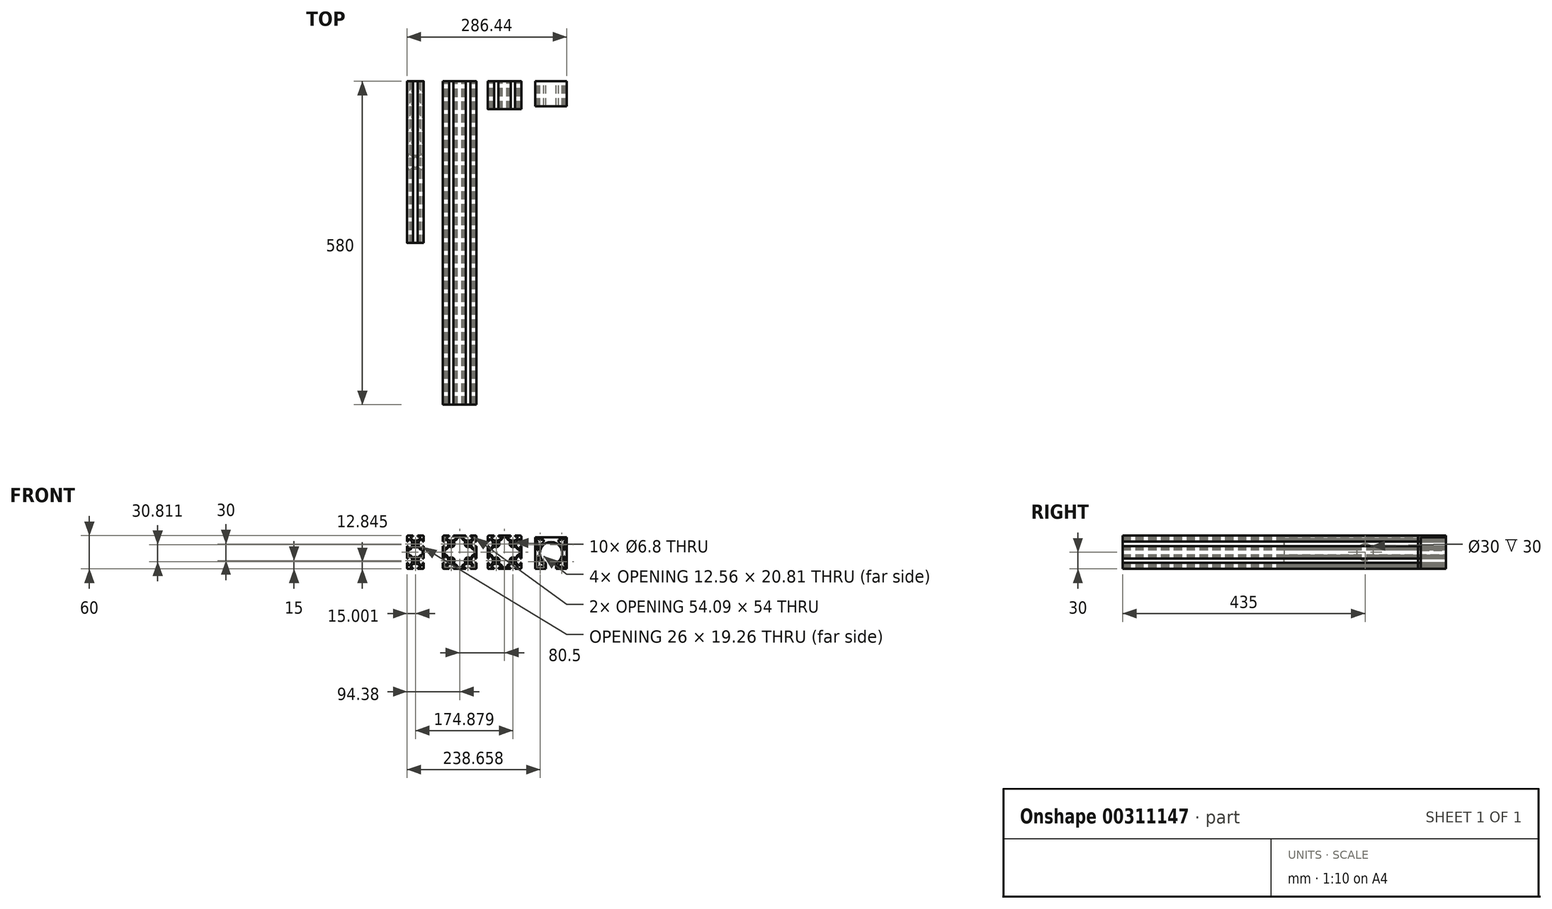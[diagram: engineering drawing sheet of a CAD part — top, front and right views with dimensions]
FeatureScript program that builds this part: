
annotation { "Feature Type Name" : "Feature", "Feature Type Description" : "" }
export const myFeature = defineFeature(function(context is Context, id is Id, definition is map)
    precondition{}
    {
        {
            var Q0;
            Q0=qCreatedBy(makeId("Front.planeOp"),FACE);
            var sketch = newSketch(context, id + "F0", { "sketchPlane" : qUnion([Q0])});
            skLineSegment(sketch, "E0.bottom", {"start": v(-15, 15) * mm, "end": v(15, 15) * mm, "construction": true});
            skLineSegment(sketch, "E0.top", {"start": v(-15, -15) * mm, "end": v(15, -15) * mm, "construction": true});
            skLineSegment(sketch, "E0.left", {"start": v(-15, 15) * mm, "end": v(-15, -15) * mm, "construction": true});
            skLineSegment(sketch, "E0.right", {"start": v(15, 15) * mm, "end": v(15, -15) * mm, "construction": true});
            skCircle(sketch, "E1", {"center": v(-15, 15) * mm, "radius": 3.4 * mm});
            skCircle(sketch, "E2", {"center": v(15, 15) * mm, "radius": 3.4 * mm});
            skCircle(sketch, "E3", {"center": v(15, -15) * mm, "radius": 3.4 * mm});
            skCircle(sketch, "E4", {"center": v(-15, -15) * mm, "radius": 3.4 * mm});
            skLineSegment(sketch, "E5", {"start": v(-28, 30) * mm, "end": v(-19, 30) * mm});
            skLineSegment(sketch, "E6", {"start": v(-19, 30) * mm, "end": v(-19, 28) * mm});
            skLineSegment(sketch, "E7", {"start": v(-19, 28) * mm, "end": v(-23.25, 28) * mm});
            skLineSegment(sketch, "E8", {"start": v(-23.25, 28) * mm, "end": v(-23.25, 25) * mm});
            skLineSegment(sketch, "E9", {"start": v(-23.25, 25) * mm, "end": v(-19, 21) * mm});
            skLineSegment(sketch, "E10.MirrorCS", {"start": v(-11, 30) * mm, "end": v(-11, 28) * mm});
            skLineSegment(sketch, "E11.MirrorCS", {"start": v(-11, 28) * mm, "end": v(-6.75, 28) * mm});
            skLineSegment(sketch, "E12.MirrorCS", {"start": v(-6.75, 28) * mm, "end": v(-6.75, 25) * mm});
            skLineSegment(sketch, "E13.MirrorCS", {"start": v(-6.75, 25) * mm, "end": v(-11, 21) * mm});
            skLineSegment(sketch, "E14", {"start": v(-19, 21) * mm, "end": v(-11, 21) * mm});
            skLineSegment(sketch, "E15", {"start": v(-4.08, 0) * mm, "end": v(-10, 0) * mm, "construction": true});
            skLineSegment(sketch, "E16", {"start": v(0, -4) * mm, "end": v(0, -10.45) * mm, "construction": true});
            skLineSegment(sketch, "E17.MirrorCS", {"start": v(19, 30) * mm, "end": v(19, 28) * mm});
            skLineSegment(sketch, "E18.MirrorCS", {"start": v(11, 30) * mm, "end": v(11, 28) * mm});
            skLineSegment(sketch, "E19.MirrorCS", {"start": v(23.25, 28) * mm, "end": v(23.25, 25) * mm});
            skLineSegment(sketch, "E20.MirrorCS", {"start": v(28, 30) * mm, "end": v(19, 30) * mm});
            skLineSegment(sketch, "E21.MirrorCS", {"start": v(19, 21) * mm, "end": v(11, 21) * mm});
            skLineSegment(sketch, "E22.MirrorCS", {"start": v(23.25, 25) * mm, "end": v(19, 21) * mm});
            skLineSegment(sketch, "E23.MirrorCS", {"start": v(6.75, 28) * mm, "end": v(6.75, 25) * mm});
            skLineSegment(sketch, "E24.MirrorCS", {"start": v(19, 28) * mm, "end": v(23.25, 28) * mm});
            skLineSegment(sketch, "E25.MirrorCS", {"start": v(6.75, 25) * mm, "end": v(11, 21) * mm});
            skLineSegment(sketch, "E26.MirrorCS", {"start": v(11, 28) * mm, "end": v(6.75, 28) * mm});
            skLineSegment(sketch, "E27.MirrorCS", {"start": v(19, -30) * mm, "end": v(19, -28) * mm});
            skLineSegment(sketch, "E28.MirrorCS", {"start": v(-19, -30) * mm, "end": v(-19, -28) * mm});
            skLineSegment(sketch, "E29.MirrorCS", {"start": v(-11, -30) * mm, "end": v(-11, -28) * mm});
            skLineSegment(sketch, "E30.MirrorCS", {"start": v(11, -30) * mm, "end": v(11, -28) * mm});
            skLineSegment(sketch, "E31.MirrorCS", {"start": v(23.25, -28) * mm, "end": v(23.25, -25) * mm});
            skLineSegment(sketch, "E32.MirrorCS", {"start": v(-28, -30) * mm, "end": v(-19, -30) * mm});
            skLineSegment(sketch, "E33.MirrorCS", {"start": v(19, -21) * mm, "end": v(11, -21) * mm});
            skLineSegment(sketch, "E34.MirrorCS", {"start": v(-19, -28) * mm, "end": v(-23.25, -28) * mm});
            skLineSegment(sketch, "E35.MirrorCS", {"start": v(6.75, -28) * mm, "end": v(6.75, -25) * mm});
            skLineSegment(sketch, "E36.MirrorCS", {"start": v(-23.25, -25) * mm, "end": v(-19, -21) * mm});
            skLineSegment(sketch, "E37.MirrorCS", {"start": v(-11, -28) * mm, "end": v(-6.75, -28) * mm});
            skLineSegment(sketch, "E38.MirrorCS", {"start": v(6.75, -25) * mm, "end": v(11, -21) * mm});
            skLineSegment(sketch, "E39.MirrorCS", {"start": v(-6.75, -25) * mm, "end": v(-11, -21) * mm});
            skLineSegment(sketch, "E40.MirrorCS", {"start": v(28, -30) * mm, "end": v(19, -30) * mm});
            skLineSegment(sketch, "E41.MirrorCS", {"start": v(-6.75, -28) * mm, "end": v(-6.75, -25) * mm});
            skLineSegment(sketch, "E42.MirrorCS", {"start": v(-19, -21) * mm, "end": v(-11, -21) * mm});
            skLineSegment(sketch, "E43.MirrorCS", {"start": v(19, -28) * mm, "end": v(23.25, -28) * mm});
            skLineSegment(sketch, "E44.MirrorCS", {"start": v(11, -28) * mm, "end": v(6.75, -28) * mm});
            skLineSegment(sketch, "E45.MirrorCS", {"start": v(23.25, -25) * mm, "end": v(19, -21) * mm});
            skLineSegment(sketch, "E46.MirrorCS", {"start": v(-23.25, -28) * mm, "end": v(-23.25, -25) * mm});
            skLineSegment(sketch, "E47", {"start": v(-30, 28) * mm, "end": v(-30, 19) * mm});
            skLineSegment(sketch, "E48", {"start": v(-30, 19) * mm, "end": v(-28, 19) * mm});
            skLineSegment(sketch, "E49", {"start": v(-28, 19) * mm, "end": v(-28, 23.25) * mm});
            skLineSegment(sketch, "E50", {"start": v(-28, 23.25) * mm, "end": v(-25, 23.25) * mm});
            skLineSegment(sketch, "E51", {"start": v(-25, 23.25) * mm, "end": v(-21, 19) * mm});
            skLineSegment(sketch, "E52.MirrorCS", {"start": v(-30, 11) * mm, "end": v(-28, 11) * mm});
            skLineSegment(sketch, "E53.MirrorCS", {"start": v(-28, 11) * mm, "end": v(-28, 6.75) * mm});
            skLineSegment(sketch, "E54.MirrorCS", {"start": v(-28, 6.75) * mm, "end": v(-25, 6.75) * mm});
            skLineSegment(sketch, "E55.MirrorCS", {"start": v(-25, 6.75) * mm, "end": v(-21, 11) * mm});
            skLineSegment(sketch, "E56", {"start": v(-21, 11) * mm, "end": v(-21, 19) * mm});
            skLineSegment(sketch, "E57.MirrorCS", {"start": v(-28, -6.75) * mm, "end": v(-25, -6.75) * mm});
            skLineSegment(sketch, "E58.MirrorCS", {"start": v(-28, -11) * mm, "end": v(-28, -6.75) * mm});
            skLineSegment(sketch, "E59.MirrorCS", {"start": v(-25, -6.75) * mm, "end": v(-21, -11) * mm});
            skLineSegment(sketch, "E60.MirrorCS", {"start": v(-21, -11) * mm, "end": v(-21, -19) * mm});
            skLineSegment(sketch, "E61.MirrorCS", {"start": v(-25, -23.25) * mm, "end": v(-21, -19) * mm});
            skLineSegment(sketch, "E62.MirrorCS", {"start": v(-28, -23.25) * mm, "end": v(-25, -23.25) * mm});
            skLineSegment(sketch, "E63.MirrorCS", {"start": v(-28, -19) * mm, "end": v(-28, -23.25) * mm});
            skLineSegment(sketch, "E64.MirrorCS", {"start": v(-30, -19) * mm, "end": v(-28, -19) * mm});
            skLineSegment(sketch, "E65.MirrorCS", {"start": v(-30, -11) * mm, "end": v(-28, -11) * mm});
            skLineSegment(sketch, "E66.MirrorCS", {"start": v(30, -11) * mm, "end": v(28, -11) * mm});
            skLineSegment(sketch, "E67.MirrorCS", {"start": v(28, -11) * mm, "end": v(28, -6.75) * mm});
            skLineSegment(sketch, "E68.MirrorCS", {"start": v(28, -6.75) * mm, "end": v(25, -6.75) * mm});
            skLineSegment(sketch, "E69.MirrorCS", {"start": v(25, -6.75) * mm, "end": v(21, -11) * mm});
            skLineSegment(sketch, "E70.MirrorCS", {"start": v(21, -11) * mm, "end": v(21, -19) * mm});
            skLineSegment(sketch, "E71.MirrorCS", {"start": v(25, -23.25) * mm, "end": v(21, -19) * mm});
            skLineSegment(sketch, "E72.MirrorCS", {"start": v(28, -23.25) * mm, "end": v(25, -23.25) * mm});
            skLineSegment(sketch, "E73.MirrorCS", {"start": v(28, -19) * mm, "end": v(28, -23.25) * mm});
            skLineSegment(sketch, "E74.MirrorCS", {"start": v(30, -19) * mm, "end": v(28, -19) * mm});
            skLineSegment(sketch, "E75.MirrorCS", {"start": v(28, 6.75) * mm, "end": v(25, 6.75) * mm});
            skLineSegment(sketch, "E76.MirrorCS", {"start": v(28, 11) * mm, "end": v(28, 6.75) * mm});
            skLineSegment(sketch, "E77.MirrorCS", {"start": v(30, 11) * mm, "end": v(28, 11) * mm});
            skLineSegment(sketch, "E78.MirrorCS", {"start": v(30, 19) * mm, "end": v(28, 19) * mm});
            skLineSegment(sketch, "E79.MirrorCS", {"start": v(28, 19) * mm, "end": v(28, 23.25) * mm});
            skLineSegment(sketch, "E80.MirrorCS", {"start": v(28, 23.25) * mm, "end": v(25, 23.25) * mm});
            skLineSegment(sketch, "E81.MirrorCS", {"start": v(25, 23.25) * mm, "end": v(21, 19) * mm});
            skLineSegment(sketch, "E82.MirrorCS", {"start": v(21, 11) * mm, "end": v(21, 19) * mm});
            skLineSegment(sketch, "E83.MirrorCS", {"start": v(25, 6.75) * mm, "end": v(21, 11) * mm});
            skLineSegment(sketch, "E84", {"start": v(-11, 30) * mm, "end": v(11, 30) * mm});
            skLineSegment(sketch, "E85", {"start": v(-30, 11) * mm, "end": v(-30, -11) * mm});
            skLineSegment(sketch, "E86", {"start": v(-30, -19) * mm, "end": v(-30, -28) * mm});
            skLineSegment(sketch, "E87", {"start": v(-11, -30) * mm, "end": v(11, -30) * mm});
            skLineSegment(sketch, "E88", {"start": v(30, -28) * mm, "end": v(30, -19) * mm});
            skLineSegment(sketch, "E89", {"start": v(30, -11) * mm, "end": v(30, 11) * mm});
            skLineSegment(sketch, "E90", {"start": v(30, 28) * mm, "end": v(30, 19) * mm});
            skLineSegment(sketch, "E91", {"start": v(-4.25, 27) * mm, "end": v(4.25, 27) * mm});
            skLineSegment(sketch, "E92", {"start": v(-4.25, 24.4) * mm, "end": v(-10.38, 18.63) * mm});
            skLineSegment(sketch, "E93", {"start": v(-4.25, 24.4) * mm, "end": v(-4.25, 27) * mm});
            skLineSegment(sketch, "E94.MirrorCS", {"start": v(4.25, 24.4) * mm, "end": v(10.38, 18.63) * mm});
            skLineSegment(sketch, "E95.MirrorCS", {"start": v(4.25, 24.4) * mm, "end": v(4.25, 27) * mm});
            skLineSegment(sketch, "E96.MirrorCS", {"start": v(-4.25, -24.4) * mm, "end": v(-10.38, -18.63) * mm});
            skLineSegment(sketch, "E97.MirrorCS", {"start": v(-4.25, -24.4) * mm, "end": v(-4.25, -27) * mm});
            skLineSegment(sketch, "E98.MirrorCS", {"start": v(-4.25, -27) * mm, "end": v(4.25, -27) * mm});
            skLineSegment(sketch, "E99.MirrorCS", {"start": v(4.25, -24.4) * mm, "end": v(4.25, -27) * mm});
            skLineSegment(sketch, "E100.MirrorCS", {"start": v(4.25, -24.4) * mm, "end": v(10.38, -18.63) * mm});
            skLineSegment(sketch, "E101", {"start": v(-27.04, -4.24) * mm, "end": v(-27.04, 4.26) * mm});
            skLineSegment(sketch, "E102", {"start": v(-24.45, -4.24) * mm, "end": v(-18.68, -10.37) * mm});
            skLineSegment(sketch, "E103", {"start": v(-24.45, -4.24) * mm, "end": v(-27.04, -4.24) * mm});
            skLineSegment(sketch, "E104.MirrorCS", {"start": v(-24.45, 4.26) * mm, "end": v(-18.68, 10.39) * mm});
            skLineSegment(sketch, "E105.MirrorCS", {"start": v(-24.45, 4.26) * mm, "end": v(-27.04, 4.26) * mm});
            skLineSegment(sketch, "E106.MirrorCS", {"start": v(27.04, -4.24) * mm, "end": v(27.04, 4.26) * mm});
            skLineSegment(sketch, "E107.MirrorCS", {"start": v(24.45, 4.26) * mm, "end": v(27.04, 4.26) * mm});
            skLineSegment(sketch, "E108.MirrorCS", {"start": v(24.45, 4.26) * mm, "end": v(18.68, 10.39) * mm});
            skLineSegment(sketch, "E109.MirrorCS", {"start": v(24.45, -4.24) * mm, "end": v(27.04, -4.24) * mm});
            skLineSegment(sketch, "E110.MirrorCS", {"start": v(24.45, -4.24) * mm, "end": v(18.68, -10.37) * mm});
            skArc(sketch, "E111", {"start": v(-18.68, 10.39) * mm, "mid": v(-10.85, 10.8) * mm, "end": v(-10.38, 18.63) * mm});
            skArc(sketch, "E112", {"start": v(10.38, 18.63) * mm, "mid": v(10.87, 10.83) * mm, "end": v(18.68, 10.39) * mm});
            skArc(sketch, "E113", {"start": v(18.68, -10.37) * mm, "mid": v(10.87, -10.83) * mm, "end": v(10.38, -18.63) * mm});
            skArc(sketch, "E114", {"start": v(-10.38, -18.63) * mm, "mid": v(-10.79, -10.75) * mm, "end": v(-18.68, -10.37) * mm});
            skLineSegment(sketch, "E115.bottom", {"start": v(65.5, 15) * mm, "end": v(95.5, 15) * mm, "construction": true});
            skLineSegment(sketch, "E115.top", {"start": v(65.5, -15) * mm, "end": v(95.5, -15) * mm, "construction": true});
            skLineSegment(sketch, "E115.left", {"start": v(65.5, 15) * mm, "end": v(65.5, -15) * mm, "construction": true});
            skLineSegment(sketch, "E115.right", {"start": v(95.5, 15) * mm, "end": v(95.5, -15) * mm, "construction": true});
            skCircle(sketch, "E116", {"center": v(65.5, 15) * mm, "radius": 3.4 * mm});
            skCircle(sketch, "E117", {"center": v(95.5, 15) * mm, "radius": 3.4 * mm});
            skCircle(sketch, "E118", {"center": v(95.5, -15) * mm, "radius": 3.4 * mm});
            skCircle(sketch, "E119", {"center": v(65.5, -15) * mm, "radius": 3.4 * mm});
            skLineSegment(sketch, "E120", {"start": v(52.5, 30) * mm, "end": v(61.5, 30) * mm});
            skLineSegment(sketch, "E121", {"start": v(61.5, 30) * mm, "end": v(61.5, 28) * mm});
            skLineSegment(sketch, "E122", {"start": v(61.5, 28) * mm, "end": v(57.25, 28) * mm});
            skLineSegment(sketch, "E123", {"start": v(57.25, 28) * mm, "end": v(57.25, 25) * mm});
            skLineSegment(sketch, "E124", {"start": v(57.25, 25) * mm, "end": v(61.5, 21) * mm});
            skLineSegment(sketch, "E125.MirrorCS", {"start": v(69.5, 30) * mm, "end": v(69.5, 28) * mm});
            skLineSegment(sketch, "E126.MirrorCS", {"start": v(69.5, 28) * mm, "end": v(73.75, 28) * mm});
            skLineSegment(sketch, "E127.MirrorCS", {"start": v(73.75, 28) * mm, "end": v(73.75, 25) * mm});
            skLineSegment(sketch, "E128.MirrorCS", {"start": v(73.75, 25) * mm, "end": v(69.5, 21) * mm});
            skLineSegment(sketch, "E129", {"start": v(61.5, 21) * mm, "end": v(69.5, 21) * mm});
            skLineSegment(sketch, "E130", {"start": v(76.42, 0) * mm, "end": v(70.5, 0) * mm, "construction": true});
            skLineSegment(sketch, "E131", {"start": v(80.5, -4) * mm, "end": v(80.5, -10.45) * mm, "construction": true});
            skLineSegment(sketch, "E132.MirrorCS", {"start": v(99.5, 30) * mm, "end": v(99.5, 28) * mm});
            skLineSegment(sketch, "E133.MirrorCS", {"start": v(91.5, 30) * mm, "end": v(91.5, 28) * mm});
            skLineSegment(sketch, "E134.MirrorCS", {"start": v(103.75, 28) * mm, "end": v(103.75, 25) * mm});
            skLineSegment(sketch, "E135.MirrorCS", {"start": v(108.5, 30) * mm, "end": v(99.5, 30) * mm});
            skLineSegment(sketch, "E136.MirrorCS", {"start": v(99.5, 21) * mm, "end": v(91.5, 21) * mm});
            skLineSegment(sketch, "E137.MirrorCS", {"start": v(103.75, 25) * mm, "end": v(99.5, 21) * mm});
            skLineSegment(sketch, "E138.MirrorCS", {"start": v(87.25, 28) * mm, "end": v(87.25, 25) * mm});
            skLineSegment(sketch, "E139.MirrorCS", {"start": v(99.5, 28) * mm, "end": v(103.75, 28) * mm});
            skLineSegment(sketch, "E140.MirrorCS", {"start": v(87.25, 25) * mm, "end": v(91.5, 21) * mm});
            skLineSegment(sketch, "E141.MirrorCS", {"start": v(91.5, 28) * mm, "end": v(87.25, 28) * mm});
            skLineSegment(sketch, "E142.MirrorCS", {"start": v(99.5, -30) * mm, "end": v(99.5, -28) * mm});
            skLineSegment(sketch, "E143.MirrorCS", {"start": v(61.5, -30) * mm, "end": v(61.5, -28) * mm});
            skLineSegment(sketch, "E144.MirrorCS", {"start": v(69.5, -30) * mm, "end": v(69.5, -28) * mm});
            skLineSegment(sketch, "E145.MirrorCS", {"start": v(91.5, -30) * mm, "end": v(91.5, -28) * mm});
            skLineSegment(sketch, "E146.MirrorCS", {"start": v(103.75, -28) * mm, "end": v(103.75, -25) * mm});
            skLineSegment(sketch, "E147.MirrorCS", {"start": v(52.5, -30) * mm, "end": v(61.5, -30) * mm});
            skLineSegment(sketch, "E148.MirrorCS", {"start": v(99.5, -21) * mm, "end": v(91.5, -21) * mm});
            skLineSegment(sketch, "E149.MirrorCS", {"start": v(61.5, -28) * mm, "end": v(57.25, -28) * mm});
            skLineSegment(sketch, "E150.MirrorCS", {"start": v(87.25, -28) * mm, "end": v(87.25, -25) * mm});
            skLineSegment(sketch, "E151.MirrorCS", {"start": v(57.25, -25) * mm, "end": v(61.5, -21) * mm});
            skLineSegment(sketch, "E152.MirrorCS", {"start": v(69.5, -28) * mm, "end": v(73.75, -28) * mm});
            skLineSegment(sketch, "E153.MirrorCS", {"start": v(87.25, -25) * mm, "end": v(91.5, -21) * mm});
            skLineSegment(sketch, "E154.MirrorCS", {"start": v(73.75, -25) * mm, "end": v(69.5, -21) * mm});
            skLineSegment(sketch, "E155.MirrorCS", {"start": v(108.5, -30) * mm, "end": v(99.5, -30) * mm});
            skLineSegment(sketch, "E156.MirrorCS", {"start": v(73.75, -28) * mm, "end": v(73.75, -25) * mm});
            skLineSegment(sketch, "E157.MirrorCS", {"start": v(61.5, -21) * mm, "end": v(69.5, -21) * mm});
            skLineSegment(sketch, "E158.MirrorCS", {"start": v(99.5, -28) * mm, "end": v(103.75, -28) * mm});
            skLineSegment(sketch, "E159.MirrorCS", {"start": v(91.5, -28) * mm, "end": v(87.25, -28) * mm});
            skLineSegment(sketch, "E160.MirrorCS", {"start": v(103.75, -25) * mm, "end": v(99.5, -21) * mm});
            skLineSegment(sketch, "E161.MirrorCS", {"start": v(57.25, -28) * mm, "end": v(57.25, -25) * mm});
            skLineSegment(sketch, "E162", {"start": v(50.5, 28) * mm, "end": v(50.5, 19) * mm});
            skLineSegment(sketch, "E163", {"start": v(50.5, 19) * mm, "end": v(52.5, 19) * mm});
            skLineSegment(sketch, "E164", {"start": v(52.5, 19) * mm, "end": v(52.5, 23.25) * mm});
            skLineSegment(sketch, "E165", {"start": v(52.5, 23.25) * mm, "end": v(55.5, 23.25) * mm});
            skLineSegment(sketch, "E166", {"start": v(55.5, 23.25) * mm, "end": v(59.5, 19) * mm});
            skLineSegment(sketch, "E167.MirrorCS", {"start": v(50.5, 11) * mm, "end": v(52.5, 11) * mm});
            skLineSegment(sketch, "E168.MirrorCS", {"start": v(52.5, 11) * mm, "end": v(52.5, 6.75) * mm});
            skLineSegment(sketch, "E169.MirrorCS", {"start": v(52.5, 6.75) * mm, "end": v(55.5, 6.75) * mm});
            skLineSegment(sketch, "E170.MirrorCS", {"start": v(55.5, 6.75) * mm, "end": v(59.5, 11) * mm});
            skLineSegment(sketch, "E171", {"start": v(59.5, 11) * mm, "end": v(59.5, 19) * mm});
            skLineSegment(sketch, "E172.MirrorCS", {"start": v(52.5, -6.75) * mm, "end": v(55.5, -6.75) * mm});
            skLineSegment(sketch, "E173.MirrorCS", {"start": v(52.5, -11) * mm, "end": v(52.5, -6.75) * mm});
            skLineSegment(sketch, "E174.MirrorCS", {"start": v(55.5, -6.75) * mm, "end": v(59.5, -11) * mm});
            skLineSegment(sketch, "E175.MirrorCS", {"start": v(59.5, -11) * mm, "end": v(59.5, -19) * mm});
            skLineSegment(sketch, "E176.MirrorCS", {"start": v(55.5, -23.25) * mm, "end": v(59.5, -19) * mm});
            skLineSegment(sketch, "E177.MirrorCS", {"start": v(52.5, -23.25) * mm, "end": v(55.5, -23.25) * mm});
            skLineSegment(sketch, "E178.MirrorCS", {"start": v(52.5, -19) * mm, "end": v(52.5, -23.25) * mm});
            skLineSegment(sketch, "E179.MirrorCS", {"start": v(50.5, -19) * mm, "end": v(52.5, -19) * mm});
            skLineSegment(sketch, "E180.MirrorCS", {"start": v(50.5, -11) * mm, "end": v(52.5, -11) * mm});
            skLineSegment(sketch, "E181.MirrorCS", {"start": v(110.5, -11) * mm, "end": v(108.5, -11) * mm});
            skLineSegment(sketch, "E182.MirrorCS", {"start": v(108.5, -11) * mm, "end": v(108.5, -6.75) * mm});
            skLineSegment(sketch, "E183.MirrorCS", {"start": v(108.5, -6.75) * mm, "end": v(105.5, -6.75) * mm});
            skLineSegment(sketch, "E184.MirrorCS", {"start": v(105.5, -6.75) * mm, "end": v(101.5, -11) * mm});
            skLineSegment(sketch, "E185.MirrorCS", {"start": v(101.5, -11) * mm, "end": v(101.5, -19) * mm});
            skLineSegment(sketch, "E186.MirrorCS", {"start": v(105.5, -23.25) * mm, "end": v(101.5, -19) * mm});
            skLineSegment(sketch, "E187.MirrorCS", {"start": v(108.5, -23.25) * mm, "end": v(105.5, -23.25) * mm});
            skLineSegment(sketch, "E188.MirrorCS", {"start": v(108.5, -19) * mm, "end": v(108.5, -23.25) * mm});
            skLineSegment(sketch, "E189.MirrorCS", {"start": v(110.5, -19) * mm, "end": v(108.5, -19) * mm});
            skLineSegment(sketch, "E190.MirrorCS", {"start": v(108.5, 6.75) * mm, "end": v(105.5, 6.75) * mm});
            skLineSegment(sketch, "E191.MirrorCS", {"start": v(108.5, 11) * mm, "end": v(108.5, 6.75) * mm});
            skLineSegment(sketch, "E192.MirrorCS", {"start": v(110.5, 11) * mm, "end": v(108.5, 11) * mm});
            skLineSegment(sketch, "E193.MirrorCS", {"start": v(110.5, 19) * mm, "end": v(108.5, 19) * mm});
            skLineSegment(sketch, "E194.MirrorCS", {"start": v(108.5, 19) * mm, "end": v(108.5, 23.25) * mm});
            skLineSegment(sketch, "E195.MirrorCS", {"start": v(108.5, 23.25) * mm, "end": v(105.5, 23.25) * mm});
            skLineSegment(sketch, "E196.MirrorCS", {"start": v(105.5, 23.25) * mm, "end": v(101.5, 19) * mm});
            skLineSegment(sketch, "E197.MirrorCS", {"start": v(101.5, 11) * mm, "end": v(101.5, 19) * mm});
            skLineSegment(sketch, "E198.MirrorCS", {"start": v(105.5, 6.75) * mm, "end": v(101.5, 11) * mm});
            skLineSegment(sketch, "E199", {"start": v(69.5, 30) * mm, "end": v(91.5, 30) * mm});
            skLineSegment(sketch, "E200", {"start": v(50.5, 11) * mm, "end": v(50.5, -11) * mm});
            skLineSegment(sketch, "E201", {"start": v(50.5, -19) * mm, "end": v(50.5, -28) * mm});
            skLineSegment(sketch, "E202", {"start": v(69.5, -30) * mm, "end": v(91.5, -30) * mm});
            skLineSegment(sketch, "E203", {"start": v(110.5, -28) * mm, "end": v(110.5, -19) * mm});
            skLineSegment(sketch, "E204", {"start": v(110.5, -11) * mm, "end": v(110.5, 11) * mm});
            skLineSegment(sketch, "E205", {"start": v(110.5, 28) * mm, "end": v(110.5, 19) * mm});
            skLineSegment(sketch, "E206", {"start": v(76.25, 27) * mm, "end": v(84.75, 27) * mm});
            skLineSegment(sketch, "E207", {"start": v(76.25, 24.4) * mm, "end": v(70.12, 18.63) * mm});
            skLineSegment(sketch, "E208", {"start": v(76.25, 24.4) * mm, "end": v(76.25, 27) * mm});
            skLineSegment(sketch, "E209.MirrorCS", {"start": v(84.75, 24.4) * mm, "end": v(90.88, 18.63) * mm});
            skLineSegment(sketch, "E210.MirrorCS", {"start": v(84.75, 24.4) * mm, "end": v(84.75, 27) * mm});
            skLineSegment(sketch, "E211.MirrorCS", {"start": v(76.25, -24.4) * mm, "end": v(70.12, -18.63) * mm});
            skLineSegment(sketch, "E212.MirrorCS", {"start": v(76.25, -24.4) * mm, "end": v(76.25, -27) * mm});
            skLineSegment(sketch, "E213.MirrorCS", {"start": v(76.25, -27) * mm, "end": v(84.75, -27) * mm});
            skLineSegment(sketch, "E214.MirrorCS", {"start": v(84.75, -24.4) * mm, "end": v(84.75, -27) * mm});
            skLineSegment(sketch, "E215.MirrorCS", {"start": v(84.75, -24.4) * mm, "end": v(90.88, -18.63) * mm});
            skLineSegment(sketch, "E216", {"start": v(53.46, -4.24) * mm, "end": v(53.46, 4.26) * mm});
            skLineSegment(sketch, "E217", {"start": v(56.05, -4.24) * mm, "end": v(61.82, -10.37) * mm});
            skLineSegment(sketch, "E218", {"start": v(56.05, -4.24) * mm, "end": v(53.46, -4.24) * mm});
            skLineSegment(sketch, "E219.MirrorCS", {"start": v(56.05, 4.26) * mm, "end": v(61.82, 10.39) * mm});
            skLineSegment(sketch, "E220.MirrorCS", {"start": v(56.05, 4.26) * mm, "end": v(53.46, 4.26) * mm});
            skLineSegment(sketch, "E221.MirrorCS", {"start": v(107.54, -4.24) * mm, "end": v(107.54, 4.26) * mm});
            skLineSegment(sketch, "E222.MirrorCS", {"start": v(104.95, 4.26) * mm, "end": v(107.54, 4.26) * mm});
            skLineSegment(sketch, "E223.MirrorCS", {"start": v(104.95, 4.26) * mm, "end": v(99.18, 10.39) * mm});
            skLineSegment(sketch, "E224.MirrorCS", {"start": v(104.95, -4.24) * mm, "end": v(107.54, -4.24) * mm});
            skLineSegment(sketch, "E225.MirrorCS", {"start": v(104.95, -4.24) * mm, "end": v(99.18, -10.37) * mm});
            skArc(sketch, "E226", {"start": v(61.82, 10.39) * mm, "mid": v(69.65, 10.8) * mm, "end": v(70.12, 18.63) * mm});
            skArc(sketch, "E227", {"start": v(90.88, 18.63) * mm, "mid": v(91.37, 10.83) * mm, "end": v(99.18, 10.39) * mm});
            skArc(sketch, "E228", {"start": v(99.18, -10.37) * mm, "mid": v(91.37, -10.83) * mm, "end": v(90.88, -18.63) * mm});
            skArc(sketch, "E229", {"start": v(70.12, -18.63) * mm, "mid": v(69.71, -10.75) * mm, "end": v(61.82, -10.37) * mm});
            skPoint(sketch, "E230.visualSharp", {"position": v(-30, 30) * mm});
            skArc(sketch, "E230.filletArc", {"start": v(-28, 30) * mm, "mid": v(-29.41, 29.41) * mm, "end": v(-30, 28) * mm});
            skPoint(sketch, "E231.visualSharp", {"position": v(30, 30) * mm});
            skArc(sketch, "E231.filletArc", {"start": v(30, 28) * mm, "mid": v(29.41, 29.41) * mm, "end": v(28, 30) * mm});
            skPoint(sketch, "E232.visualSharp", {"position": v(30, -30) * mm});
            skArc(sketch, "E232.filletArc", {"start": v(28, -30) * mm, "mid": v(29.41, -29.41) * mm, "end": v(30, -28) * mm});
            skPoint(sketch, "E233.visualSharp", {"position": v(-30, -30) * mm});
            skArc(sketch, "E233.filletArc", {"start": v(-30, -28) * mm, "mid": v(-29.41, -29.41) * mm, "end": v(-28, -30) * mm});
            skPoint(sketch, "E234.visualSharp", {"position": v(50.5, -30) * mm});
            skArc(sketch, "E234.filletArc", {"start": v(50.5, -28) * mm, "mid": v(51.09, -29.41) * mm, "end": v(52.5, -30) * mm});
            skPoint(sketch, "E235.visualSharp", {"position": v(50.5, 30) * mm});
            skArc(sketch, "E235.filletArc", {"start": v(52.5, 30) * mm, "mid": v(51.09, 29.41) * mm, "end": v(50.5, 28) * mm});
            skPoint(sketch, "E236.visualSharp", {"position": v(110.5, 30) * mm});
            skArc(sketch, "E236.filletArc", {"start": v(110.5, 28) * mm, "mid": v(109.91, 29.41) * mm, "end": v(108.5, 30) * mm});
            skPoint(sketch, "E237.visualSharp", {"position": v(110.5, -30) * mm});
            skArc(sketch, "E237.filletArc", {"start": v(108.5, -30) * mm, "mid": v(109.91, -29.41) * mm, "end": v(110.5, -28) * mm});
            skPoint(sketch, "E238.firstSnap0", {"position": v(-23.5, 30) * mm});
            skLineSegment(sketch, "E239", {"start": v(-92.38, 30) * mm, "end": v(-83.38, 30) * mm});
            skLineSegment(sketch, "E240", {"start": v(-83.38, 30) * mm, "end": v(-83.38, 28) * mm});
            skLineSegment(sketch, "E241", {"start": v(-83.38, 28) * mm, "end": v(-87.63, 28) * mm});
            skLineSegment(sketch, "E242", {"start": v(-87.63, 28) * mm, "end": v(-87.63, 25) * mm});
            skLineSegment(sketch, "E243", {"start": v(-66.38, 30) * mm, "end": v(-75.38, 30) * mm});
            skLineSegment(sketch, "E244", {"start": v(-75.38, 30) * mm, "end": v(-75.38, 28) * mm});
            skLineSegment(sketch, "E245", {"start": v(-75.38, 28) * mm, "end": v(-71.13, 28) * mm});
            skLineSegment(sketch, "E246", {"start": v(-71.13, 28) * mm, "end": v(-71.13, 25) * mm});
            skLineSegment(sketch, "E247", {"start": v(-83.38, 21) * mm, "end": v(-75.1, 21) * mm});
            skLineSegment(sketch, "E248", {"start": v(-83.38, 21) * mm, "end": v(-87.63, 25) * mm});
            skLineSegment(sketch, "E249", {"start": v(-75.1, 21) * mm, "end": v(-71.13, 25) * mm});
            skPoint(sketch, "E250.startSnap0", {"position": v(-79.38, -30) * mm});
            skLineSegment(sketch, "E251", {"start": v(-72.98, 0) * mm, "end": v(-85.14, 0) * mm, "construction": true});
            skPoint(sketch, "E251.startSnap0", {"position": v(-64.38, 0) * mm});
            skPoint(sketch, "E251.endSnap0", {"position": v(-64.38, 0) * mm});
            skLineSegment(sketch, "E252.MirrorCS", {"start": v(-83.38, -30) * mm, "end": v(-83.38, -28) * mm});
            skLineSegment(sketch, "E253.MirrorCS", {"start": v(-87.63, -28) * mm, "end": v(-87.63, -25) * mm});
            skLineSegment(sketch, "E254.MirrorCS", {"start": v(-75.38, -30) * mm, "end": v(-75.38, -28) * mm});
            skLineSegment(sketch, "E255.MirrorCS", {"start": v(-71.13, -28) * mm, "end": v(-71.13, -25) * mm});
            skLineSegment(sketch, "E256.MirrorCS", {"start": v(-83.38, -28) * mm, "end": v(-87.63, -28) * mm});
            skLineSegment(sketch, "E257.MirrorCS", {"start": v(-75.38, -28) * mm, "end": v(-71.13, -28) * mm});
            skLineSegment(sketch, "E258.MirrorCS", {"start": v(-83.38, -21) * mm, "end": v(-75.1, -21) * mm});
            skLineSegment(sketch, "E259.MirrorCS", {"start": v(-83.38, -21) * mm, "end": v(-87.63, -25) * mm});
            skLineSegment(sketch, "E260.MirrorCS", {"start": v(-75.1, -21) * mm, "end": v(-71.13, -25) * mm});
            skLineSegment(sketch, "E261.MirrorCS", {"start": v(-92.38, -30) * mm, "end": v(-83.38, -30) * mm});
            skLineSegment(sketch, "E262.MirrorCS", {"start": v(-66.38, -30) * mm, "end": v(-75.38, -30) * mm});
            skLineSegment(sketch, "E263", {"start": v(-94.38, 28) * mm, "end": v(-94.38, 19) * mm});
            skLineSegment(sketch, "E264", {"start": v(-94.38, 19) * mm, "end": v(-92.38, 19) * mm});
            skLineSegment(sketch, "E265", {"start": v(-92.38, 19) * mm, "end": v(-92.38, 23.25) * mm});
            skLineSegment(sketch, "E266", {"start": v(-92.38, 23.25) * mm, "end": v(-89.38, 23.25) * mm});
            skLineSegment(sketch, "E267.MirrorCS", {"start": v(-92.38, -23.25) * mm, "end": v(-89.38, -23.25) * mm});
            skLineSegment(sketch, "E268.MirrorCS", {"start": v(-92.38, -19) * mm, "end": v(-92.38, -23.25) * mm});
            skLineSegment(sketch, "E269.MirrorCS", {"start": v(-94.38, -19) * mm, "end": v(-92.38, -19) * mm});
            skLineSegment(sketch, "E270.MirrorCS", {"start": v(-94.38, -28) * mm, "end": v(-94.38, -19) * mm});
            skLineSegment(sketch, "E271", {"start": v(-85.38, 19) * mm, "end": v(-85.38, 11) * mm});
            skLineSegment(sketch, "E272", {"start": v(-85.38, 19) * mm, "end": v(-89.38, 23.25) * mm});
            skLineSegment(sketch, "E273", {"start": v(-94.38, 11) * mm, "end": v(-92.38, 11) * mm});
            skLineSegment(sketch, "E274", {"start": v(-92.38, 11) * mm, "end": v(-92.38, 6.75) * mm});
            skLineSegment(sketch, "E275", {"start": v(-92.38, 6.75) * mm, "end": v(-89.38, 6.75) * mm});
            skLineSegment(sketch, "E276", {"start": v(-89.38, 6.75) * mm, "end": v(-85.38, 11) * mm});
            skLineSegment(sketch, "E277.MirrorCS", {"start": v(-92.38, -11) * mm, "end": v(-92.38, -6.75) * mm});
            skLineSegment(sketch, "E278.MirrorCS", {"start": v(-94.38, -11) * mm, "end": v(-92.38, -11) * mm});
            skLineSegment(sketch, "E279.MirrorCS", {"start": v(-89.38, -6.75) * mm, "end": v(-85.38, -11) * mm});
            skLineSegment(sketch, "E280.MirrorCS", {"start": v(-92.38, -6.75) * mm, "end": v(-89.38, -6.75) * mm});
            skLineSegment(sketch, "E281.MirrorCS", {"start": v(-85.38, -19) * mm, "end": v(-85.38, -11) * mm});
            skLineSegment(sketch, "E282.MirrorCS", {"start": v(-85.38, -19) * mm, "end": v(-89.38, -23.25) * mm});
            skLineSegment(sketch, "E283", {"start": v(-94.38, 11) * mm, "end": v(-94.38, -11) * mm});
            skLineSegment(sketch, "E284.MirrorCS", {"start": v(-64.38, -11) * mm, "end": v(-66.38, -11) * mm});
            skLineSegment(sketch, "E285.MirrorCS", {"start": v(-64.38, 11) * mm, "end": v(-66.38, 11) * mm});
            skLineSegment(sketch, "E286.MirrorCS", {"start": v(-64.38, -28) * mm, "end": v(-64.38, -19) * mm});
            skLineSegment(sketch, "E287.MirrorCS", {"start": v(-64.38, -19) * mm, "end": v(-66.38, -19) * mm});
            skLineSegment(sketch, "E288.MirrorCS", {"start": v(-66.38, -19) * mm, "end": v(-66.38, -23.25) * mm});
            skLineSegment(sketch, "E289.MirrorCS", {"start": v(-64.38, 19) * mm, "end": v(-66.38, 19) * mm});
            skLineSegment(sketch, "E290.MirrorCS", {"start": v(-66.38, 19) * mm, "end": v(-66.38, 23.25) * mm});
            skLineSegment(sketch, "E291.MirrorCS", {"start": v(-66.38, -11) * mm, "end": v(-66.38, -6.75) * mm});
            skLineSegment(sketch, "E292.MirrorCS", {"start": v(-69.38, 6.75) * mm, "end": v(-73.38, 11) * mm});
            skLineSegment(sketch, "E293.MirrorCS", {"start": v(-66.38, 6.75) * mm, "end": v(-69.38, 6.75) * mm});
            skLineSegment(sketch, "E294.MirrorCS", {"start": v(-66.38, 11) * mm, "end": v(-66.38, 6.75) * mm});
            skLineSegment(sketch, "E295.MirrorCS", {"start": v(-73.38, 19) * mm, "end": v(-69.38, 23.25) * mm});
            skLineSegment(sketch, "E296.MirrorCS", {"start": v(-73.38, 19) * mm, "end": v(-73.38, 11) * mm});
            skLineSegment(sketch, "E297.MirrorCS", {"start": v(-64.38, 11) * mm, "end": v(-64.38, -11) * mm});
            skLineSegment(sketch, "E298.MirrorCS", {"start": v(-69.38, -6.75) * mm, "end": v(-73.38, -11) * mm});
            skLineSegment(sketch, "E299.MirrorCS", {"start": v(-66.38, -6.75) * mm, "end": v(-69.38, -6.75) * mm});
            skLineSegment(sketch, "E300.MirrorCS", {"start": v(-73.38, -19) * mm, "end": v(-73.38, -11) * mm});
            skLineSegment(sketch, "E301.MirrorCS", {"start": v(-64.38, 28) * mm, "end": v(-64.38, 19) * mm});
            skLineSegment(sketch, "E302.MirrorCS", {"start": v(-73.38, -19) * mm, "end": v(-69.38, -23.25) * mm});
            skLineSegment(sketch, "E303.MirrorCS", {"start": v(-66.38, 23.25) * mm, "end": v(-69.38, 23.25) * mm});
            skLineSegment(sketch, "E304.MirrorCS", {"start": v(-66.38, -23.25) * mm, "end": v(-69.38, -23.25) * mm});
            skCircle(sketch, "E305", {"center": v(-79.38, 15) * mm, "radius": 3.4 * mm});
            skPoint(sketch, "E305.centerSnap0", {"position": v(-85.38, 15) * mm});
            skCircle(sketch, "E306.MirrorC", {"center": v(-79.38, -15) * mm, "radius": 3.4 * mm});
            skLineSegment(sketch, "E307", {"start": v(-79.38, 4.43) * mm, "end": v(-79.38, -3.53) * mm, "construction": true});
            skLineSegment(sketch, "E308", {"start": v(-92.38, 4.75) * mm, "end": v(-92.38, -4.75) * mm});
            skLineSegment(sketch, "E309.0", {"start": v(-88.51, 4.75) * mm, "end": v(-83.92, 9.63) * mm});
            skLineSegment(sketch, "E309.1", {"start": v(-92.38, 4.75) * mm, "end": v(-88.51, 4.75) * mm});
            skLineSegment(sketch, "E310.0", {"start": v(-88.51, -4.75) * mm, "end": v(-83.92, -9.63) * mm});
            skLineSegment(sketch, "E310.1", {"start": v(-92.38, -4.75) * mm, "end": v(-88.51, -4.75) * mm});
            skLineSegment(sketch, "E311.MirrorCS", {"start": v(-70.24, 4.75) * mm, "end": v(-74.83, 9.63) * mm});
            skLineSegment(sketch, "E312.MirrorCS", {"start": v(-66.38, 4.75) * mm, "end": v(-70.24, 4.75) * mm});
            skLineSegment(sketch, "E313.MirrorCS", {"start": v(-66.38, 4.75) * mm, "end": v(-66.38, -4.75) * mm});
            skLineSegment(sketch, "E314.MirrorCS", {"start": v(-66.38, -4.75) * mm, "end": v(-70.24, -4.75) * mm});
            skLineSegment(sketch, "E315.MirrorCS", {"start": v(-70.24, -4.75) * mm, "end": v(-74.83, -9.63) * mm});
            skArc(sketch, "E316", {"start": v(-83.92, 9.63) * mm, "mid": v(-79.38, 8.7) * mm, "end": v(-74.83, 9.63) * mm});
            skArc(sketch, "E317.MirrorCS", {"start": v(-83.92, -9.63) * mm, "mid": v(-79.38, -8.7) * mm, "end": v(-74.83, -9.63) * mm});
            skPoint(sketch, "E318.visualSharp", {"position": v(-94.38, 30) * mm});
            skArc(sketch, "E318.filletArc", {"start": v(-92.38, 30) * mm, "mid": v(-93.8, 29.41) * mm, "end": v(-94.38, 28) * mm});
            skPoint(sketch, "E319.visualSharp", {"position": v(-64.38, 30) * mm});
            skArc(sketch, "E319.filletArc", {"start": v(-64.38, 28) * mm, "mid": v(-64.96, 29.41) * mm, "end": v(-66.38, 30) * mm});
            skPoint(sketch, "E320.visualSharp", {"position": v(-64.38, -30) * mm});
            skArc(sketch, "E320.filletArc", {"start": v(-66.38, -30) * mm, "mid": v(-64.96, -29.41) * mm, "end": v(-64.38, -28) * mm});
            skPoint(sketch, "E321.visualSharp", {"position": v(-94.38, -30) * mm});
            skArc(sketch, "E321.filletArc", {"start": v(-94.38, -28) * mm, "mid": v(-93.8, -29.41) * mm, "end": v(-92.38, -30) * mm});
            skLineSegment(sketch, "E322", {"start": v(135.56, -30) * mm, "end": v(135.56, 26.5) * mm});
            skLineSegment(sketch, "E323", {"start": v(135.56, 26.5) * mm, "end": v(192.06, 26.5) * mm});
            skLineSegment(sketch, "E324", {"start": v(192.06, 26.5) * mm, "end": v(192.06, -30) * mm});
            skLineSegment(sketch, "E325", {"start": v(192.06, -30) * mm, "end": v(173.06, -30) * mm});
            skLineSegment(sketch, "E326", {"start": v(135.56, -30) * mm, "end": v(154.56, -30) * mm});
            skPoint(sketch, "E327.centerSnap0", {"position": v(135.56, -1.75) * mm});
            skPoint(sketch, "E327.centerSnap1", {"position": v(163.8, 26.5) * mm});
            skLineSegment(sketch, "E328", {"start": v(154.56, -30) * mm, "end": v(154.56, -19.48) * mm});
            skLineSegment(sketch, "E329", {"start": v(173.06, -30) * mm, "end": v(173.06, -19.48) * mm});
            skArc(sketch, "E330", {"start": v(154.56, -19.48) * mm, "mid": v(163.8, 18.25) * mm, "end": v(173.06, -19.48) * mm});
            skLineSegment(sketch, "E331", {"start": v(139.56, -16.75) * mm, "end": v(139.56, -6.75) * mm, "construction": true});
            skLineSegment(sketch, "E332", {"start": v(163.8, -1.75) * mm, "end": v(163.8, -8.48) * mm});
            skLineSegment(sketch, "E333", {"start": v(163.8, -1.75) * mm, "end": v(156.05, -1.75) * mm});
            skLineSegment(sketch, "E334", {"start": v(139.56, -6.75) * mm, "end": v(139.56, -23) * mm});
            skLineSegment(sketch, "E335", {"start": v(139.56, -6.75) * mm, "end": v(140.34, -6.75) * mm});
            skLineSegment(sketch, "E336", {"start": v(142.56, -26) * mm, "end": v(150.56, -26) * mm});
            skLineSegment(sketch, "E337", {"start": v(150.56, -26) * mm, "end": v(150.56, -21.76) * mm});
            skArc(sketch, "E338", {"start": v(139.56, -23) * mm, "mid": v(138.63, -26.93) * mm, "end": v(142.56, -26) * mm});
            skArc(sketch, "E339", {"start": v(150.56, -21.76) * mm, "mid": v(143.97, -15.26) * mm, "end": v(140.34, -6.75) * mm});
            skLineSegment(sketch, "E340.MirrorCS", {"start": v(177.06, -26) * mm, "end": v(177.06, -21.76) * mm});
            skLineSegment(sketch, "E341.MirrorCS", {"start": v(185.06, -26) * mm, "end": v(177.06, -26) * mm});
            skArc(sketch, "E342.MirrorCS", {"start": v(188.06, -23) * mm, "mid": v(188.99, -26.93) * mm, "end": v(185.06, -26) * mm});
            skLineSegment(sketch, "E343.MirrorCS", {"start": v(188.06, -6.75) * mm, "end": v(188.06, -23) * mm});
            skLineSegment(sketch, "E344.MirrorCS", {"start": v(188.06, -6.75) * mm, "end": v(187.28, -6.75) * mm});
            skLineSegment(sketch, "E345.MirrorCS", {"start": v(139.56, 3.25) * mm, "end": v(139.56, 19.5) * mm});
            skArc(sketch, "E346.MirrorCS", {"start": v(139.56, 19.5) * mm, "mid": v(138.63, 23.43) * mm, "end": v(142.56, 22.5) * mm});
            skLineSegment(sketch, "E347.MirrorCS", {"start": v(142.56, 22.5) * mm, "end": v(150.56, 22.5) * mm});
            skLineSegment(sketch, "E348.MirrorCS", {"start": v(150.56, 22.5) * mm, "end": v(150.56, 18.26) * mm});
            skLineSegment(sketch, "E349.MirrorCS", {"start": v(139.56, 3.25) * mm, "end": v(140.34, 3.25) * mm});
            skArc(sketch, "E350.MirrorCS", {"start": v(150.56, 18.26) * mm, "mid": v(143.97, 11.76) * mm, "end": v(140.34, 3.25) * mm});
            skArc(sketch, "E351.MirrorCS", {"start": v(177.06, -21.76) * mm, "mid": v(183.65, -15.26) * mm, "end": v(187.28, -6.75) * mm});
            skArc(sketch, "E352.MirrorCS", {"start": v(177.06, 18.26) * mm, "mid": v(183.65, 11.76) * mm, "end": v(187.28, 3.25) * mm});
            skLineSegment(sketch, "E353.MirrorCS", {"start": v(188.06, 3.25) * mm, "end": v(187.28, 3.25) * mm});
            skLineSegment(sketch, "E354.MirrorCS", {"start": v(188.06, 3.25) * mm, "end": v(188.06, 19.5) * mm});
            skLineSegment(sketch, "E355.MirrorCS", {"start": v(177.06, 22.5) * mm, "end": v(177.06, 18.26) * mm});
            skLineSegment(sketch, "E356.MirrorCS", {"start": v(185.06, 22.5) * mm, "end": v(177.06, 22.5) * mm});
            skArc(sketch, "E357.MirrorCS", {"start": v(188.06, 19.5) * mm, "mid": v(188.99, 23.43) * mm, "end": v(185.06, 22.5) * mm});
            skSolve(sketch);
        }
        {
            var Q0;
            Q0=makeQuery(id+"F0.imprint","IMPRINT",FACE,{"disambiguationData":[TD([[makeQuery(id+"F0.imprint","IMPRINT",EDGE,{"derivedFrom":sQuery(id+"F0.wireOp",EDGE,"E1")}),-1.0]])]});
            extrude(context, id + "F1", {"entities" : qUnion([Q0]), "depth" : 580 * mm});
        }
        {
            var Q0;
            Q0=makeQuery(id+"F0.imprint","IMPRINT",FACE,{"disambiguationData":[TD([[makeQuery(id+"F0.imprint","IMPRINT",EDGE,{"derivedFrom":sQuery(id+"F0.wireOp",EDGE,"E116")}),-1.0]])]});
            extrude(context, id + "F2", {"entities" : qUnion([Q0]), "depth" : 50 * mm});
        }
        {
            var Q0;
            Q0=makeQuery(id+"F0.imprint","IMPRINT",FACE,{"disambiguationData":[TD([[makeQuery(id+"F0.imprint","IMPRINT",EDGE,{"derivedFrom":sQuery(id+"F0.wireOp",EDGE,"E239")}),-1.0]])]});
            extrude(context, id + "F3", {"entities" : qUnion([Q0]), "depth" : 290 * mm});
        }
        {
            var Q0;
            Q0=makeQuery(id+"F3.opExtrude","SWEPT_FACE",FACE,{"disambiguationData":[OSD([sQuery(id+"F0.wireOp",EDGE,"E283")])]});
            var sketch = newSketch(context, id + "F4", { "sketchPlane" : qUnion([Q0])});
            skCircle(sketch, "E358", {"center": v(145, 0) * mm, "radius": 15 * mm});
            skPoint(sketch, "E358.centerSnap0", {"position": v(145, 11) * mm});
            skSolve(sketch);
        }
        {
            var Q0;
            {var subQ0=sQuery(id+"F4.wireOp",EDGE,"E358");var subQ1=sQuery(id+"F0.wireOp",EDGE,"E283");var subQ2=makeQuery(id+"F3.opExtrude","SWEPT_EDGE",EDGE,{"disambiguationData":[OSD([sQuery(id+"F0.wireOp",EDGE,"E273"),subQ1])]});var subQ3=makeQuery(id+"F4.imprint","INTERSECT",VERTEX,{"disambiguationData":[OD(0.0)],"derivedFrom":[subQ2,subQ0]});Q0=makeQuery(id+"F4.imprint","IMPRINT",FACE,{"disambiguationData":[TD([[makeQuery(id+"F4.imprint","IMPRINT",EDGE,{"disambiguationData":[TD([[subQ3,-1.0]])],"derivedFrom":subQ0}),1.0]])]});}
            var Q1;
            {var subQ0=sQuery(id+"F4.wireOp",EDGE,"E358");var subQ1=makeQuery(id+"F3.opExtrude","SWEPT_EDGE",EDGE,{"disambiguationData":[OSD([sQuery(id+"F0.wireOp",EDGE,"E278.MirrorCS"),sQuery(id+"F0.wireOp",EDGE,"E283")])]});var subQ2=makeQuery(id+"F4.imprint","INTERSECT",VERTEX,{"disambiguationData":[OD(0.0)],"derivedFrom":[subQ1,subQ0]});Q1=makeQuery(id+"F4.imprint","IMPRINT",FACE,{"disambiguationData":[TD([[makeQuery(id+"F4.imprint","IMPRINT",EDGE,{"disambiguationData":[TD([[subQ2,-1.0]])],"derivedFrom":subQ0}),1.0]])]});}
            var Q2;
            {var subQ0=sQuery(id+"F4.wireOp",EDGE,"E358");var subQ1=makeQuery(id+"F3.opExtrude","SWEPT_EDGE",EDGE,{"disambiguationData":[OSD([sQuery(id+"F0.wireOp",EDGE,"E273"),sQuery(id+"F0.wireOp",EDGE,"E283")])]});var subQ2=makeQuery(id+"F4.imprint","INTERSECT",VERTEX,{"disambiguationData":[OD(0.0)],"derivedFrom":[subQ1,subQ0]});Q2=makeQuery(id+"F4.imprint","IMPRINT",FACE,{"disambiguationData":[TD([[makeQuery(id+"F4.imprint","IMPRINT",EDGE,{"disambiguationData":[TD([[subQ2,1.0]])],"derivedFrom":subQ0}),1.0]])]});}
            extrude(context, id + "F5", {"entities" : qUnion([Q0, Q1, Q2]), "operationType" : NewBodyOperationType.REMOVE, "oppositeDirection" : true, "depth" : 30 * mm});
        }
        {
            var Q0;
            Q0=makeQuery(id+"F0.imprint","IMPRINT",FACE,{"disambiguationData":[TD([[makeQuery(id+"F0.imprint","IMPRINT",EDGE,{"derivedFrom":sQuery(id+"F0.wireOp",EDGE,"E322")}),-1.0]])]});
            extrude(context, id + "F6", {"entities" : qUnion([Q0]), "depth" : 45 * mm});
        }
    });
